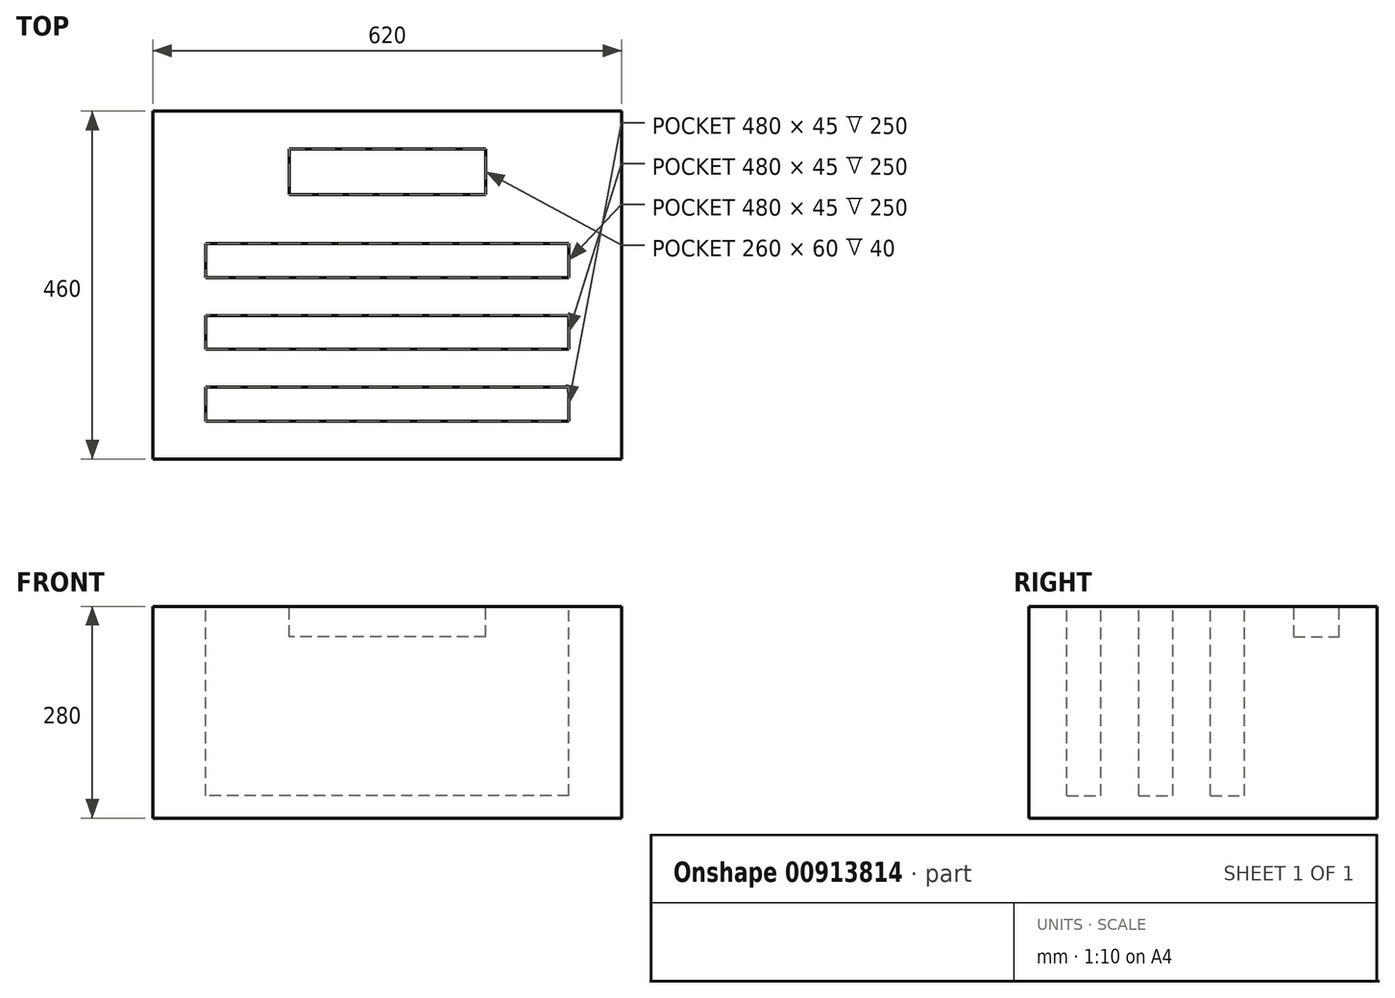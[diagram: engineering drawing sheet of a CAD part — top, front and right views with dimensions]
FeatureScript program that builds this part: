
annotation { "Feature Type Name" : "Feature", "Feature Type Description" : "" }
export const myFeature = defineFeature(function(context is Context, id is Id, definition is map)
    precondition{}
    {
        {
            var Q0;
            Q0=qCreatedBy(makeId("Top.planeOp"),FACE);
            var sketch = newSketch(context, id + "F0", { "sketchPlane" : qUnion([Q0])});
            skLineSegment(sketch, "E0.bottom", {"start": v(310, -230) * mm, "end": v(-310, -230) * mm});
            skLineSegment(sketch, "E0.top", {"start": v(310, 230) * mm, "end": v(-310, 230) * mm});
            skLineSegment(sketch, "E0.left", {"start": v(310, -230) * mm, "end": v(310, 230) * mm});
            skLineSegment(sketch, "E0.right", {"start": v(-310, -230) * mm, "end": v(-310, 230) * mm});
            skLineSegment(sketch, "E1.bottom", {"start": v(320, -240) * mm, "end": v(-320, -240) * mm});
            skLineSegment(sketch, "E1.top", {"start": v(320, 240) * mm, "end": v(-320, 240) * mm});
            skLineSegment(sketch, "E1.left", {"start": v(320, -240) * mm, "end": v(320, 240) * mm});
            skLineSegment(sketch, "E1.right", {"start": v(-320, -240) * mm, "end": v(-320, 240) * mm});
            skLineSegment(sketch, "E2.bottom", {"start": v(240, -180) * mm, "end": v(-240, -180) * mm});
            skLineSegment(sketch, "E2.top", {"start": v(240, -135) * mm, "end": v(-240, -135) * mm});
            skLineSegment(sketch, "E2.left", {"start": v(240, -180) * mm, "end": v(240, -135) * mm});
            skLineSegment(sketch, "E2.right", {"start": v(-240, -180) * mm, "end": v(-240, -135) * mm});
            skPoint(sketch, "E2.middle", {"position": v(0, 0) * mm});
            skLineSegment(sketch, "E3.0.1.0", {"start": v(240, -85) * mm, "end": v(240, -40) * mm});
            skLineSegment(sketch, "E3.0.1.1", {"start": v(240, -85) * mm, "end": v(-240, -85) * mm});
            skLineSegment(sketch, "E3.0.1.2", {"start": v(240, -40) * mm, "end": v(-240, -40) * mm});
            skLineSegment(sketch, "E3.0.1.3", {"start": v(-240, -85) * mm, "end": v(-240, -40) * mm});
            skLineSegment(sketch, "E3.0.2.0", {"start": v(240, 10) * mm, "end": v(240, 55) * mm});
            skLineSegment(sketch, "E3.0.2.1", {"start": v(240, 10) * mm, "end": v(-240, 10) * mm});
            skLineSegment(sketch, "E3.0.2.2", {"start": v(240, 55) * mm, "end": v(-240, 55) * mm});
            skLineSegment(sketch, "E3.0.2.3", {"start": v(-240, 10) * mm, "end": v(-240, 55) * mm});
            skLineSegment(sketch, "E3.direction1", {"start": v(-240, -180) * mm, "end": v(-215, -180) * mm, "construction": true});
            skLineSegment(sketch, "E3.direction2", {"start": v(-240, -180) * mm, "end": v(-240, -85) * mm, "construction": true});
            skSolve(sketch);
        }
        {
            var Q0;
            Q0=makeQuery(id+"F0.imprint","IMPRINT",FACE,{"disambiguationData":[TD([[makeQuery(id+"F0.imprint","IMPRINT",EDGE,{"derivedFrom":sQuery(id+"F0.wireOp",EDGE,"E0.bottom")}),-1.0]])]});
            var Q1;
            Q1=makeQuery(id+"F0.imprint","IMPRINT",FACE,{"disambiguationData":[TD([[makeQuery(id+"F0.imprint","IMPRINT",EDGE,{"derivedFrom":sQuery(id+"F0.wireOp",EDGE,"E3.0.2.0")}),1.0]])]});
            var Q2;
            Q2=makeQuery(id+"F0.imprint","IMPRINT",FACE,{"disambiguationData":[TD([[makeQuery(id+"F0.imprint","IMPRINT",EDGE,{"derivedFrom":sQuery(id+"F0.wireOp",EDGE,"E3.0.1.0")}),1.0]])]});
            var Q3;
            Q3=makeQuery(id+"F0.imprint","IMPRINT",FACE,{"disambiguationData":[TD([[makeQuery(id+"F0.imprint","IMPRINT",EDGE,{"derivedFrom":sQuery(id+"F0.wireOp",EDGE,"E2.bottom")}),-1.0]])]});
            extrude(context, id + "F1", {"entities" : qUnion([Q0, Q1, Q2, Q3]), "oppositeDirection" : true, "depth" : 280 * mm, "offsetDistance" : 25 * mm});
        }
        {
            var Q0;
            Q0=makeQuery(id+"F0.imprint","IMPRINT",FACE,{"disambiguationData":[TD([[makeQuery(id+"F0.imprint","IMPRINT",EDGE,{"derivedFrom":sQuery(id+"F0.wireOp",EDGE,"E3.0.2.0")}),1.0]])]});
            var Q1;
            Q1=makeQuery(id+"F0.imprint","IMPRINT",FACE,{"disambiguationData":[TD([[makeQuery(id+"F0.imprint","IMPRINT",EDGE,{"derivedFrom":sQuery(id+"F0.wireOp",EDGE,"E3.0.1.0")}),1.0]])]});
            var Q2;
            Q2=makeQuery(id+"F0.imprint","IMPRINT",FACE,{"disambiguationData":[TD([[makeQuery(id+"F0.imprint","IMPRINT",EDGE,{"derivedFrom":sQuery(id+"F0.wireOp",EDGE,"E2.bottom")}),-1.0]])]});
            extrude(context, id + "F2", {"entities" : qUnion([Q0, Q1, Q2]), "operationType" : NewBodyOperationType.REMOVE, "oppositeDirection" : true, "depth" : 250 * mm, "offsetDistance" : 25 * mm});
        }
        {
            var Q0;
            Q0=makeQuery(id+"F1.opExtrude","CAP_FACE",FACE,{"disambiguationData":[OSD([sQuery(id+"F0.wireOp",EDGE,"E0.bottom"),sQuery(id+"F0.wireOp",EDGE,"E0.top"),sQuery(id+"F0.wireOp",EDGE,"E0.left"),sQuery(id+"F0.wireOp",EDGE,"E0.right")])],"isStart":true});
            var sketch = newSketch(context, id + "F3", { "sketchPlane" : qUnion([Q0])});
            skLineSegment(sketch, "E4.bottom", {"start": v(130, 120) * mm, "end": v(-130, 120) * mm});
            skLineSegment(sketch, "E4.top", {"start": v(130, 180) * mm, "end": v(-130, 180) * mm});
            skLineSegment(sketch, "E4.left", {"start": v(130, 120) * mm, "end": v(130, 180) * mm});
            skLineSegment(sketch, "E4.right", {"start": v(-130, 120) * mm, "end": v(-130, 180) * mm});
            skPoint(sketch, "E4.middle", {"position": v(0, 150) * mm});
            skSolve(sketch);
        }
        {
            var Q0;
            Q0 = qSketchRegion(id + "F3", true);
            extrude(context, id + "F4", {"entities" : qUnion([Q0]), "operationType" : NewBodyOperationType.REMOVE, "oppositeDirection" : true, "depth" : 40 * mm, "offsetDistance" : 25 * mm});
        }
    });
